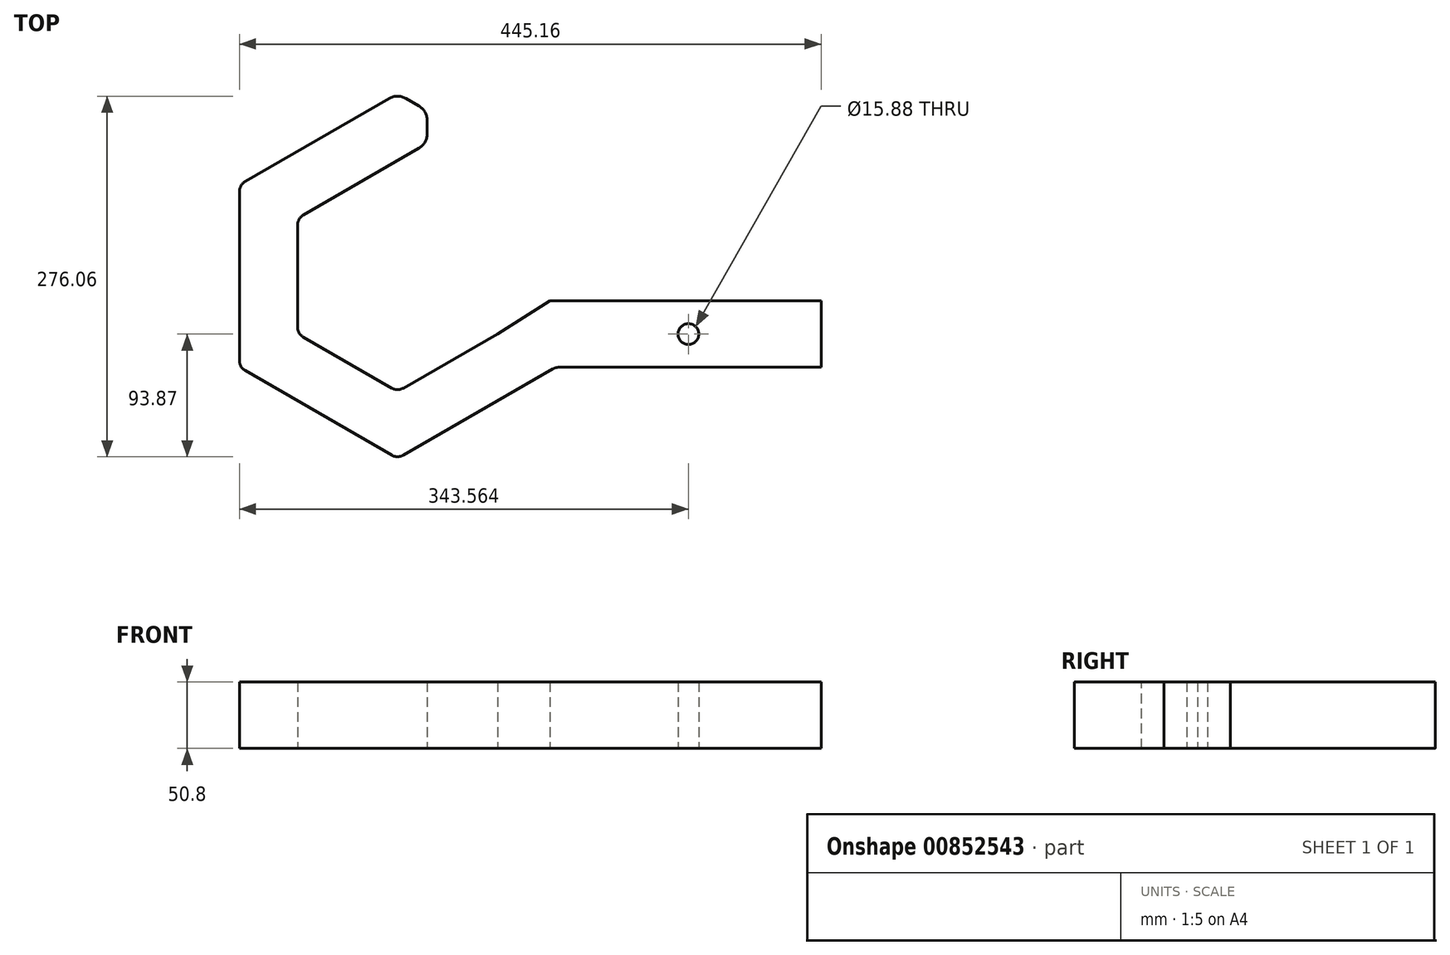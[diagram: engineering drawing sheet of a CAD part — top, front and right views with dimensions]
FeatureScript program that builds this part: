
annotation { "Feature Type Name" : "Feature", "Feature Type Description" : "" }
export const myFeature = defineFeature(function(context is Context, id is Id, definition is map)
    precondition{}
    {
        {
            var Q0;
            Q0=qCreatedBy(makeId("Top.planeOp"),FACE);
            var sketch = newSketch(context, id + "F0", { "sketchPlane" : qUnion([Q0])});
            skCircle(sketch, "E0.cCircle", {"center": v(0, 0) * mm, "radius": 139.7 * mm, "construction": true});
            skLineSegment(sketch, "E0.0", {"start": v(0, -139.7) * mm, "end": v(-120.98, -69.85) * mm});
            skLineSegment(sketch, "E0.1", {"start": v(-120.98, -69.85) * mm, "end": v(-120.98, 69.85) * mm});
            skLineSegment(sketch, "E0.2", {"start": v(-120.98, 69.85) * mm, "end": v(0, 139.7) * mm});
            skLineSegment(sketch, "E0.3", {"start": v(0, 139.7) * mm, "end": v(22.64, 126.63) * mm});
            skLineSegment(sketch, "E0.5", {"start": v(120.98, -69.85) * mm, "end": v(0, -139.7) * mm});
            skCircle(sketch, "E1.cCircle", {"center": v(0, 0) * mm, "radius": 88.37 * mm, "construction": true});
            skLineSegment(sketch, "E1.0", {"start": v(0, -88.37) * mm, "end": v(-76.53, -44.19) * mm});
            skLineSegment(sketch, "E1.1", {"start": v(-76.53, -44.19) * mm, "end": v(-76.53, 44.19) * mm});
            skLineSegment(sketch, "E1.2", {"start": v(-76.53, 44.19) * mm, "end": v(0, 88.37) * mm});
            skLineSegment(sketch, "E1.5", {"start": v(76.53, -44.19) * mm, "end": v(0, -88.37) * mm});
            skLineSegment(sketch, "E2", {"start": v(120.98, -69.85) * mm, "end": v(324.18, -69.85) * mm});
            skLineSegment(sketch, "E3", {"start": v(324.18, -69.85) * mm, "end": v(324.18, -19.05) * mm});
            skLineSegment(sketch, "E4", {"start": v(324.18, -19.05) * mm, "end": v(116.48, -19.05) * mm});
            skLineSegment(sketch, "E5", {"start": v(0, 88.37) * mm, "end": v(22.64, 101.44) * mm});
            skLineSegment(sketch, "E6", {"start": v(22.64, 101.44) * mm, "end": v(22.64, 126.63) * mm});
            skPoint(sketch, "E7.orphan", {"position": v(120.98, 69.85) * mm});
            skPoint(sketch, "E8.orphan", {"position": v(76.53, 44.19) * mm});
            skLineSegment(sketch, "E9", {"start": v(76.53, -44.19) * mm, "end": v(116.48, -19.05) * mm});
            skCircle(sketch, "E10", {"center": v(222.58, -44.45) * mm, "radius": 7.94 * mm});
            skSolve(sketch);
        }
        {
            var Q0;
            Q0=makeQuery(id+"F0.imprint","IMPRINT",FACE,{"disambiguationData":[TD([[makeQuery(id+"F0.imprint","IMPRINT",EDGE,{"derivedFrom":sQuery(id+"F0.wireOp",EDGE,"E0.0")}),-1.0]])]});
            extrude(context, id + "F1", {"entities" : qUnion([Q0]), "depth" : 50.8 * mm, "offsetDistance" : 25.4 * mm});
        }
        {
            var Q0;
            Q0=makeQuery(id+"F1.opExtrude","SWEPT_EDGE",EDGE,{"disambiguationData":[OSD([sQuery(id+"F0.wireOp",EDGE,"E0.1"),sQuery(id+"F0.wireOp",EDGE,"E0.2")])]});
            var Q1;
            Q1=makeQuery(id+"F1.opExtrude","SWEPT_EDGE",EDGE,{"disambiguationData":[OSD([sQuery(id+"F0.wireOp",EDGE,"E0.0"),sQuery(id+"F0.wireOp",EDGE,"E0.1")])]});
            var Q2;
            Q2=makeQuery(id+"F1.opExtrude","SWEPT_EDGE",EDGE,{"disambiguationData":[OSD([sQuery(id+"F0.wireOp",EDGE,"E0.0"),sQuery(id+"F0.wireOp",EDGE,"E0.5")])]});
            var Q3;
            Q3=makeQuery(id+"F1.opExtrude","SWEPT_EDGE",EDGE,{"disambiguationData":[OSD([sQuery(id+"F0.wireOp",EDGE,"E0.5"),sQuery(id+"F0.wireOp",EDGE,"E2")])]});
            var Q4;
            Q4=makeQuery(id+"F1.opExtrude","SWEPT_EDGE",EDGE,{"disambiguationData":[OSD([sQuery(id+"F0.wireOp",EDGE,"E1.1"),sQuery(id+"F0.wireOp",EDGE,"E1.2")])]});
            var Q5;
            Q5=makeQuery(id+"F1.opExtrude","SWEPT_EDGE",EDGE,{"disambiguationData":[OSD([sQuery(id+"F0.wireOp",EDGE,"E1.0"),sQuery(id+"F0.wireOp",EDGE,"E1.1")])]});
            var Q6;
            Q6=makeQuery(id+"F1.opExtrude","SWEPT_EDGE",EDGE,{"disambiguationData":[OSD([sQuery(id+"F0.wireOp",EDGE,"E1.0"),sQuery(id+"F0.wireOp",EDGE,"E1.5")])]});
            fillet(context, id + "F2", {"entities" : qUnion([Q0, Q1, Q2, Q3, Q4, Q5, Q6]), "radius" : 8.9 * mm, "tangentPropagation" : true, "allowEdgeOverflow" : false});
        }
        {
            var Q0;
            Q0=makeQuery(id+"F1.opExtrude","SWEPT_EDGE",EDGE,{"disambiguationData":[OSD([sQuery(id+"F0.wireOp",EDGE,"E0.2"),sQuery(id+"F0.wireOp",EDGE,"E0.3")])]});
            var Q1;
            Q1=makeQuery(id+"F1.opExtrude","SWEPT_EDGE",EDGE,{"disambiguationData":[OSD([sQuery(id+"F0.wireOp",EDGE,"E5"),sQuery(id+"F0.wireOp",EDGE,"E6")])]});
            var Q2;
            Q2=makeQuery(id+"F1.opExtrude","SWEPT_EDGE",EDGE,{"disambiguationData":[OSD([sQuery(id+"F0.wireOp",EDGE,"E0.3"),sQuery(id+"F0.wireOp",EDGE,"E6")])]});
            fillet(context, id + "F3", {"entities" : qUnion([Q0, Q1, Q2]), "radius" : 12.7 * mm, "tangentPropagation" : true, "allowEdgeOverflow" : false});
        }
    });
